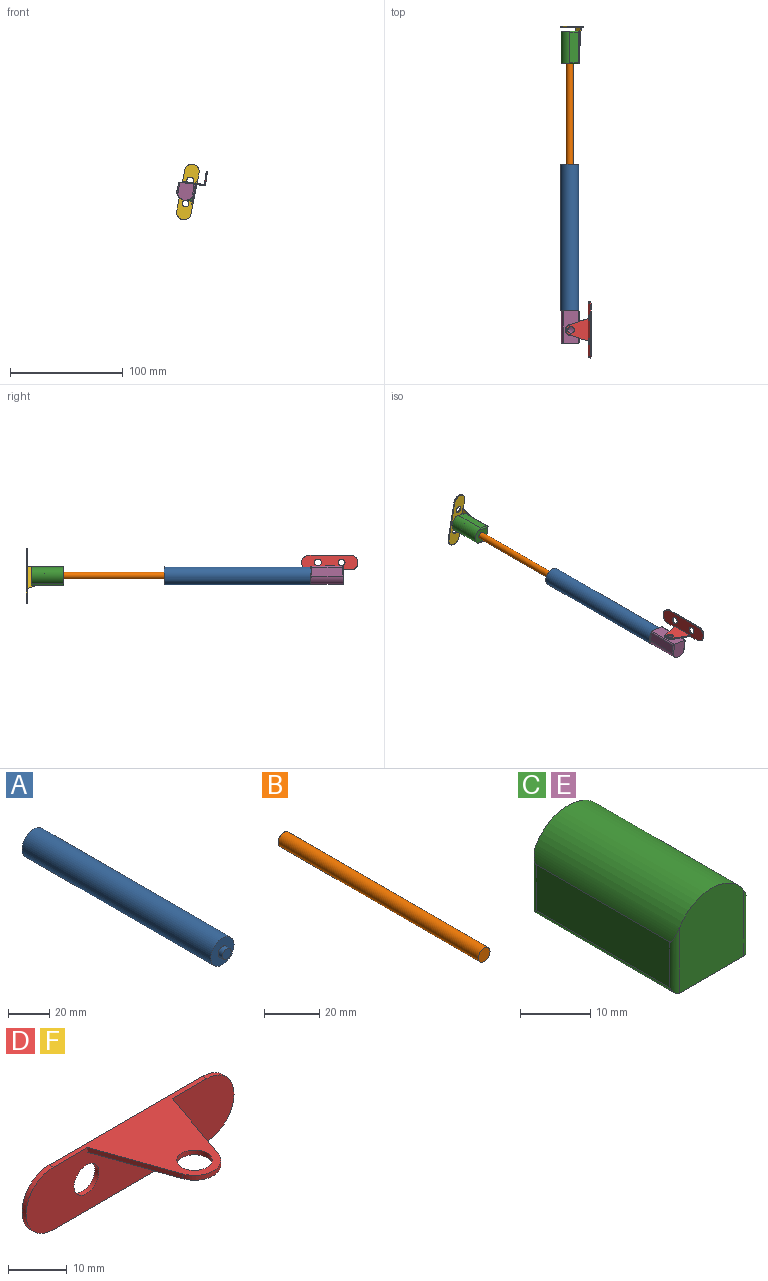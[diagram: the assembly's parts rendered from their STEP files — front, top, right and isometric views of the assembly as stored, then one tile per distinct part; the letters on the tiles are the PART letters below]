
ASSEMBLY  parts=6 mates=5
PART A: 7 faces, bbox 16x133x16 mm
  f0: cylinder r=3mm len=127mm, axis (0,1,0), area 2393.9mm2, adj f3,f6
  f1: cylinder r=8mm len=130mm, axis (0,1,0), area 6534.5mm2, adj f2,f3
  f2: plane 16x16mm, normal (0,-1,0), area 172.8mm2, adj f1,f5
  f3: plane 16x16mm, normal (0,1,0), area 172.8mm2, adj f0,f1
  f4: plane 6x6mm, normal (0,-1,0), area 28.3mm2, adj f5
  f5: cylinder r=3mm len=6mm, axis (0,1,0), area 56.5mm2, adj f2,f4
  f6: plane 6x6mm, normal (0,1,0), area 28.3mm2, adj f0
PART B: 3 faces, bbox 6x103x6 mm
  f0: cylinder r=3mm len=103mm, axis (0,1,0), area 1941.5mm2, adj f1,f2
  f1: plane 6x6mm, normal (0,-1,0), area 28.3mm2, adj f0
  f2: plane 6x6mm, normal (0,1,0), area 28.3mm2, adj f0
PART C: 16 faces, bbox 15x29x15.1 mm
  f0: cylinder r=7.65mm len=29mm, axis (0,1,0), area 606.2mm2, adj f1,f3,f4,f5,f10,f11,f13,f14
  f1: plane 27x8mm, normal (-1,0,0), area 216mm2, adj f0,f10,f11,f12
  f2: plane 29x13mm, normal (0,0,-1), area 298.5mm2, adj f4,f5,f7,f12,f15
  f3: plane 27x8mm, normal (1,0,0), area 216mm2, adj f0,f13,f14,f15
  f4: plane 15.15x13mm, normal (0,-1,0), area 183.1mm2, adj f0,f2,f10,f13
  f5: plane 15.15x13mm, normal (0,1,0), area 154.8mm2, adj f0,f2,f9,f11,f14
  f6: cone r=0mm half-angle=59deg, axis (0,0,-1), area 91.6mm2, adj f7
  f7: cylinder r=5mm len=12mm, axis (0,0,-1), area 377mm2, adj f2,f6
  f8: cone r=0mm half-angle=59deg, axis (0,1,0), area 33mm2, adj f9
  f9: cylinder r=3mm len=6mm, axis (0,1,0), area 56.5mm2, adj f5,f8
  f10: cylinder r=1mm len=11.53mm, axis (0,0,1), area 15.3mm2, adj f0,f1,f4,f12
  f11: cylinder r=1mm len=11.53mm, axis (0,0,-1), area 15.3mm2, adj f0,f1,f5,f12
  f12: cylinder r=1mm len=29mm, axis (0,1,0), area 44.4mm2, adj f1,f2,f10,f11
  f13: cylinder r=1mm len=11.53mm, axis (0,0,-1), area 15.3mm2, adj f0,f3,f4,f15
  f14: cylinder r=1mm len=11.53mm, axis (0,0,1), area 15.3mm2, adj f0,f3,f5,f15
  f15: cylinder r=1mm len=29mm, axis (0,-1,0), area 44.4mm2, adj f2,f3,f13,f14
PART D: 13 faces, bbox 50x21x13 mm
  f0: plane 50x13mm, normal (0,-1,0), area 536.9mm2, adj f2,f3,f4,f5,f6,f7,f10,f11
  f1: plane 50x13mm, normal (0,1,0), area 557.2mm2, adj f2,f3,f4,f5,f6,f7
  f2: cylinder r=6.5mm len=13mm, axis (0,1,0), area 20.4mm2, adj f0,f1,f3,f5
  f3: plane 37x1mm, normal (0,0,-1), area 37mm2, adj f0,f1,f2,f4
  f4: cylinder r=6.5mm len=13mm, axis (0,1,0), area 20.4mm2, adj f0,f1,f3,f5
  f5: plane 37x21mm, normal (0,0,1), area 272mm2, adj f0,f1,f2,f4,f8,f9,f11,f12
  f6: cylinder r=3mm len=6mm, axis (0,1,0), area 18.8mm2, adj f0,f1
  f7: cylinder r=3mm len=6mm, axis (0,1,0), area 18.8mm2, adj f0,f1
  f8: cylinder r=4.5mm len=8.5mm, axis (0,0,1), area 11.1mm2, adj f5,f10,f11,f12
  f9: cylinder r=3mm len=6mm, axis (0,0,1), area 18.8mm2, adj f5,f10
  f10: plane 20.3x20mm, normal (0,0,-1), area 235mm2, adj f0,f8,f9,f11,f12
  f11: plane 16.98x5.9mm, normal (-0.94,-0.33,0), area 18mm2, adj f0,f5,f8,f10
  f12: plane 16.98x5.9mm, normal (0.94,-0.33,0), area 18mm2, adj f0,f5,f8,f10
PART E: same geometry as C
PART F: same geometry as D
PLACE A t=(65.26,-35.02,2.93)mm fixed
PLACE B rot(axis=(0,-1,0),90deg) t=(65.26,57.98,2.93)mm
PLACE C rot(axis=(-0.64,0,0.77),180deg) t=(68.2,54.08,2.36)mm
PLACE D rot(axis=(-0.71,-0.71,0.05),174.1deg) t=(83.62,-182.02,14.39)mm
PLACE E rot(axis=(0,-1,0),171.7deg) t=(65.69,-165.02,5.9)mm
PLACE F rot(axis=(0,1,0),101deg) t=(67.22,87.58,2.55)mm
MATE revolute D.f9 <-> E.f6  axis (-0.15,0,-0.99) through (66.35,-182.02,10.35)mm
MATE revolute A.f0 <-> E.f8  axis (0,-1,0) through (65.26,-168.02,2.93)mm
MATE revolute B.f0 <-> C.f8  axis (0,1,0) through (65.26,57.98,2.93)mm
MATE cylindrical A.f0 <-> B.f0  axis (0,-1,0) through (65.26,-165.02,2.93)mm
MATE revolute F.f9 <-> C.f6  axis (-0.98,0,0.19) through (72.62,71.08,1.5)mm
